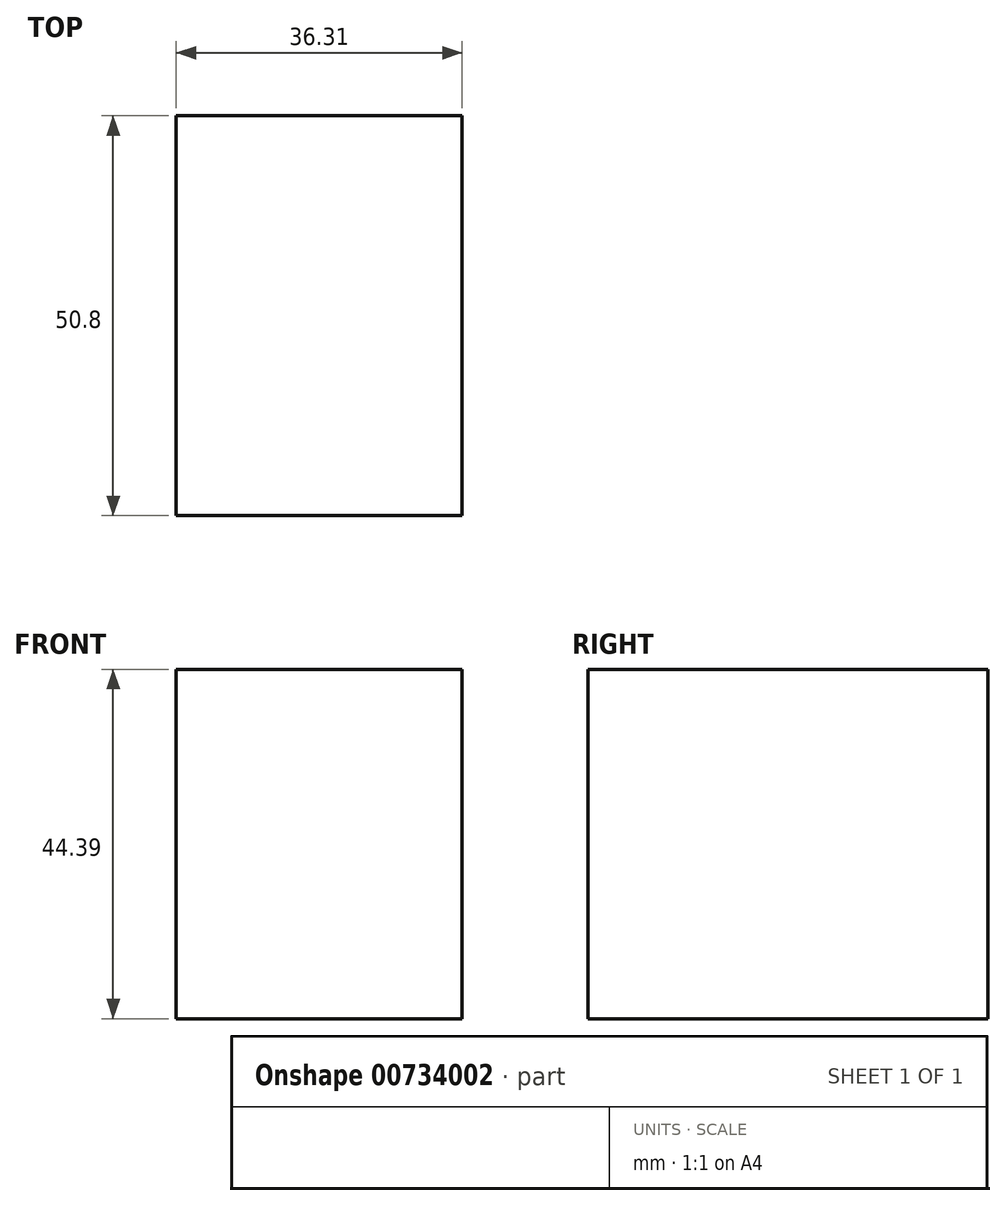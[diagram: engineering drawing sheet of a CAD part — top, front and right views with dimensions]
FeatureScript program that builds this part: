
annotation { "Feature Type Name" : "Feature", "Feature Type Description" : "" }
export const myFeature = defineFeature(function(context is Context, id is Id, definition is map)
    precondition{}
    {
        {
            var Q0;
            Q0=qCreatedBy(makeId("Front.planeOp"),FACE);
            var sketch = newSketch(context, id + "F0", { "sketchPlane" : qUnion([Q0])});
            skLineSegment(sketch, "E0.bottom", {"start": v(0, 0) * mm, "end": v(-36.31, 0) * mm});
            skLineSegment(sketch, "E0.top", {"start": v(0, -44.39) * mm, "end": v(-36.31, -44.39) * mm});
            skLineSegment(sketch, "E0.left", {"start": v(0, 0) * mm, "end": v(0, -44.39) * mm});
            skLineSegment(sketch, "E0.right", {"start": v(-36.31, 0) * mm, "end": v(-36.31, -44.39) * mm});
            skSolve(sketch);
        }
        {
            var Q0;
            Q0 = qSketchRegion(id + "F0", true);
            extrude(context, id + "F1", {"entities" : qUnion([Q0]), "depth" : 50.8 * mm, "offsetDistance" : 25.4 * mm});
        }
    });
